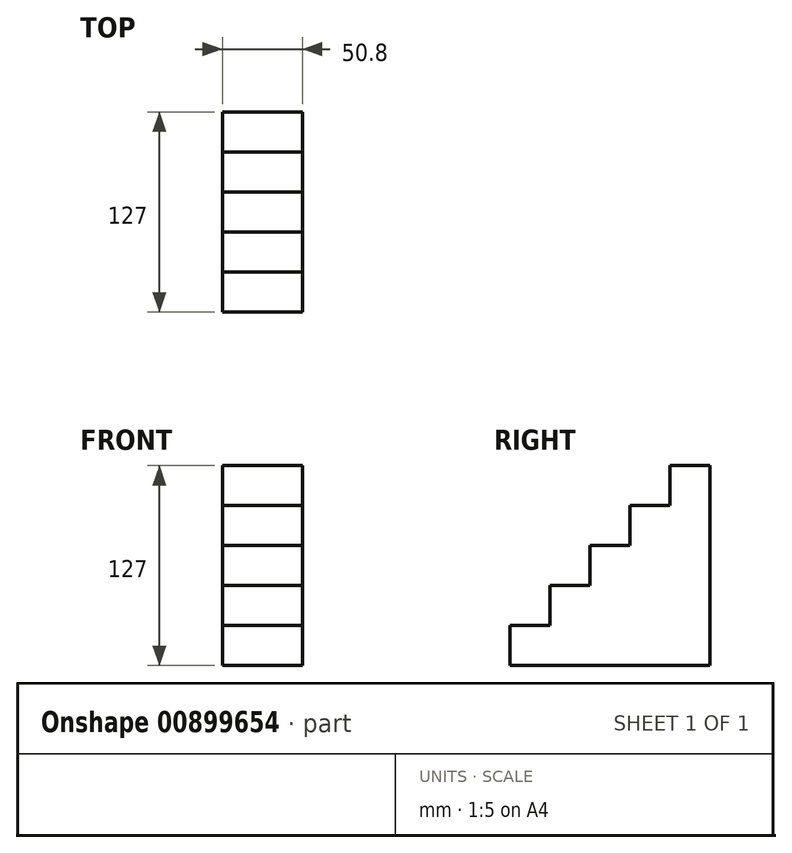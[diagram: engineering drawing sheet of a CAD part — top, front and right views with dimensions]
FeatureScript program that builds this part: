
annotation { "Feature Type Name" : "Feature", "Feature Type Description" : "" }
export const myFeature = defineFeature(function(context is Context, id is Id, definition is map)
    precondition{}
    {
        {
            var Q0;
            Q0=qCreatedBy(makeId("Top.planeOp"),FACE);
            var sketch = newSketch(context, id + "F0", { "sketchPlane" : qUnion([Q0])});
            skLineSegment(sketch, "E0", {"start": v(0, 0) * mm, "end": v(50.8, 0) * mm});
            skLineSegment(sketch, "E1", {"start": v(50.8, 0) * mm, "end": v(50.8, 50.8) * mm});
            skLineSegment(sketch, "E2", {"start": v(50.8, 50.8) * mm, "end": v(0, 50.8) * mm});
            skLineSegment(sketch, "E3", {"start": v(0, 50.8) * mm, "end": v(0, 0) * mm});
            skSolve(sketch);
        }
        {
            var Q0;
            Q0 = qSketchRegion(id + "F0", true);
            extrude(context, id + "F1", {"entities" : qUnion([Q0]), "depth" : 25.4 * mm, "offsetDistance" : 25.4 * mm});
        }
        {
            var Q0;
            Q0=makeQuery(id+"F1.opExtrude","CAP_FACE",FACE,{"disambiguationData":[OSD([sQuery(id+"F0.wireOp",EDGE,"E0"),sQuery(id+"F0.wireOp",EDGE,"E1"),sQuery(id+"F0.wireOp",EDGE,"E2"),sQuery(id+"F0.wireOp",EDGE,"E3")])],"isStart":false});
            var sketch = newSketch(context, id + "F2", { "sketchPlane" : qUnion([Q0])});
            skLineSegment(sketch, "E4", {"start": v(0, 50.8) * mm, "end": v(50.8, 50.8) * mm});
            skLineSegment(sketch, "E5", {"start": v(50.8, 50.8) * mm, "end": v(50.8, 25.4) * mm});
            skLineSegment(sketch, "E6", {"start": v(50.8, 25.4) * mm, "end": v(0, 25.4) * mm});
            skLineSegment(sketch, "E7", {"start": v(0, 25.4) * mm, "end": v(0, 50.8) * mm});
            skSolve(sketch);
        }
        {
            var Q0;
            Q0=makeQuery(id+"F2.imprint","IMPRINT",FACE,{"disambiguationData":[TD([[makeQuery(id+"F2.imprint","IMPRINT",EDGE,{"derivedFrom":sQuery(id+"F2.wireOp",EDGE,"E4")}),1.0]])]});
            extrude(context, id + "F3", {"entities" : qUnion([Q0]), "operationType" : NewBodyOperationType.ADD, "depth" : 25.4 * mm, "offsetDistance" : 25.4 * mm});
        }
        {
            var Q0;
            Q0=makeQuery(id+"F3.boolean.opBoolean","MERGE",FACE,{"derivedFrom":[makeQuery(id+"F1.opExtrude","SWEPT_FACE",FACE,{"disambiguationData":[OSD([sQuery(id+"F0.wireOp",EDGE,"E2")])]}),makeQuery(id+"F3.opExtrude","SWEPT_FACE",FACE,{"disambiguationData":[OSD([sQuery(id+"F2.wireOp",EDGE,"E4")])]})]});
            var sketch = newSketch(context, id + "F4", { "sketchPlane" : qUnion([Q0])});
            skLineSegment(sketch, "E8", {"start": v(0, 0) * mm, "end": v(-50.8, 0) * mm});
            skLineSegment(sketch, "E9", {"start": v(-50.8, 0) * mm, "end": v(-50.8, 76.2) * mm});
            skLineSegment(sketch, "E10", {"start": v(-50.8, 76.2) * mm, "end": v(0, 76.2) * mm});
            skLineSegment(sketch, "E11", {"start": v(0, 76.2) * mm, "end": v(0, 0) * mm});
            skSolve(sketch);
        }
        {
            var Q0;
            Q0 = qSketchRegion(id + "F4", true);
            extrude(context, id + "F5", {"entities" : qUnion([Q0]), "operationType" : NewBodyOperationType.ADD, "depth" : 25.4 * mm, "offsetDistance" : 25.4 * mm});
        }
        {
            var Q0;
            Q0=makeQuery(id+"F5.boolean.opBoolean","MERGE",FACE,{"derivedFrom":[makeQuery(id+"F1.opExtrude","CAP_FACE",FACE,{"disambiguationData":[OSD([sQuery(id+"F0.wireOp",EDGE,"E0"),sQuery(id+"F0.wireOp",EDGE,"E1"),sQuery(id+"F0.wireOp",EDGE,"E2"),sQuery(id+"F0.wireOp",EDGE,"E3")])],"isStart":true}),makeQuery(id+"F5.opExtrude","SWEPT_FACE",FACE,{"disambiguationData":[OSD([sQuery(id+"F4.wireOp",EDGE,"E8")])]})]});
            var sketch = newSketch(context, id + "F6", { "sketchPlane" : qUnion([Q0])});
            skLineSegment(sketch, "E12.bottom", {"start": v(50.8, -76.2) * mm, "end": v(0, -76.2) * mm});
            skLineSegment(sketch, "E12.top", {"start": v(50.8, 25.4) * mm, "end": v(0, 25.4) * mm});
            skLineSegment(sketch, "E12.left", {"start": v(50.8, -76.2) * mm, "end": v(50.8, 25.4) * mm});
            skLineSegment(sketch, "E12.right", {"start": v(0, -76.2) * mm, "end": v(0, 25.4) * mm});
            skSolve(sketch);
        }
        {
            var Q0;
            Q0 = qSketchRegion(id + "F6", true);
            extrude(context, id + "F7", {"entities" : qUnion([Q0]), "operationType" : NewBodyOperationType.ADD, "depth" : 25.4 * mm, "offsetDistance" : 25.4 * mm});
        }
        {
            var Q0;
            Q0=makeQuery(id+"F7.opExtrude","CAP_FACE",FACE,{"disambiguationData":[OSD([sQuery(id+"F6.wireOp",EDGE,"E12.bottom"),sQuery(id+"F6.wireOp",EDGE,"E12.top"),sQuery(id+"F6.wireOp",EDGE,"E12.left"),sQuery(id+"F6.wireOp",EDGE,"E12.right")])],"isStart":false});
            var sketch = newSketch(context, id + "F8", { "sketchPlane" : qUnion([Q0])});
            skLineSegment(sketch, "E13.bottom", {"start": v(50.8, -76.2) * mm, "end": v(0, -76.2) * mm});
            skLineSegment(sketch, "E13.top", {"start": v(50.8, 50.8) * mm, "end": v(0, 50.8) * mm});
            skLineSegment(sketch, "E13.left", {"start": v(50.8, -76.2) * mm, "end": v(50.8, 50.8) * mm});
            skLineSegment(sketch, "E13.right", {"start": v(0, -76.2) * mm, "end": v(0, 50.8) * mm});
            skSolve(sketch);
        }
        {
            var Q0;
            Q0 = qSketchRegion(id + "F8", true);
            extrude(context, id + "F9", {"entities" : qUnion([Q0]), "operationType" : NewBodyOperationType.ADD, "depth" : 25.4 * mm, "offsetDistance" : 25.4 * mm});
        }
    });
